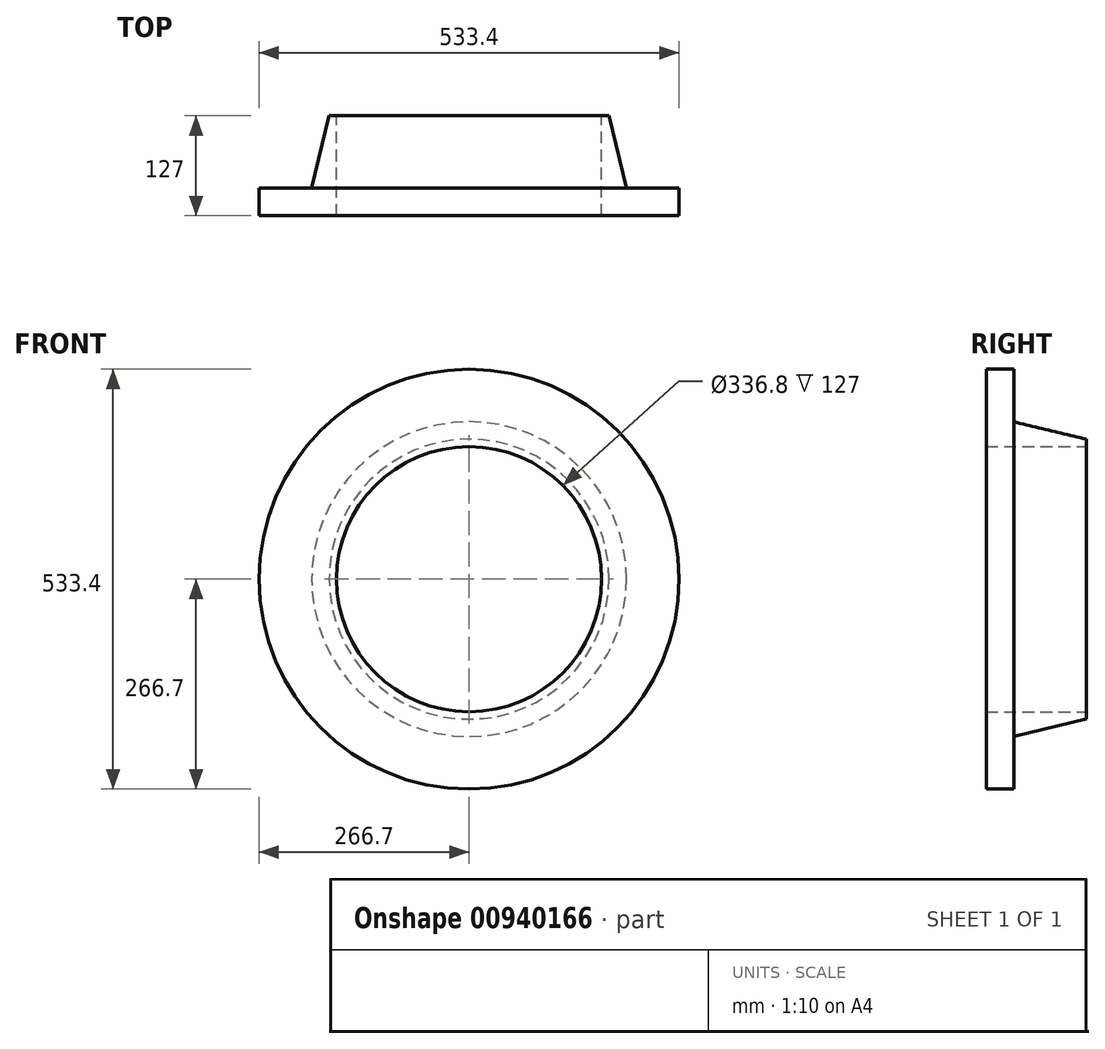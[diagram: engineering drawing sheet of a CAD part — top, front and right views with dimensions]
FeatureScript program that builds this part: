
annotation { "Feature Type Name" : "Feature", "Feature Type Description" : "" }
export const myFeature = defineFeature(function(context is Context, id is Id, definition is map)
    precondition{}
    {
        {
            var Q0;
            Q0=qCreatedBy(makeId("Top.planeOp"),FACE);
            var sketch = newSketch(context, id + "F0", { "sketchPlane" : qUnion([Q0])});
            skLineSegment(sketch, "E0", {"start": v(0, 0) * mm, "end": v(266.7, 0) * mm, "construction": true});
            skLineSegment(sketch, "E1", {"start": v(266.7, 0) * mm, "end": v(266.7, 34.93) * mm});
            skLineSegment(sketch, "E2", {"start": v(266.7, 34.93) * mm, "end": v(200.03, 34.93) * mm});
            skLineSegment(sketch, "E3", {"start": v(200.03, 34.92) * mm, "end": v(177.8, 127) * mm});
            skLineSegment(sketch, "E4", {"start": v(177.8, 127) * mm, "end": v(168.4, 127) * mm});
            skLineSegment(sketch, "E5", {"start": v(168.4, 127) * mm, "end": v(168.4, 0) * mm});
            skLineSegment(sketch, "E6", {"start": v(168.4, 0) * mm, "end": v(266.7, 0) * mm});
            skLineSegment(sketch, "E7", {"start": v(0, 127) * mm, "end": v(0, 0) * mm, "construction": true});
            skSolve(sketch);
        }
        {
            var Q0;
            Q0=qSketchRegion(id+"F0",true);
            var Q1;
            Q1=sQuery(id+"F0.wireOp",EDGE,"E7");
            revolve(context, id + "F1", {"entities" : qUnion([Q0]), "axis" : qUnion([Q1]), "revolveType" : RevolveType.FULL});
        }
    });
